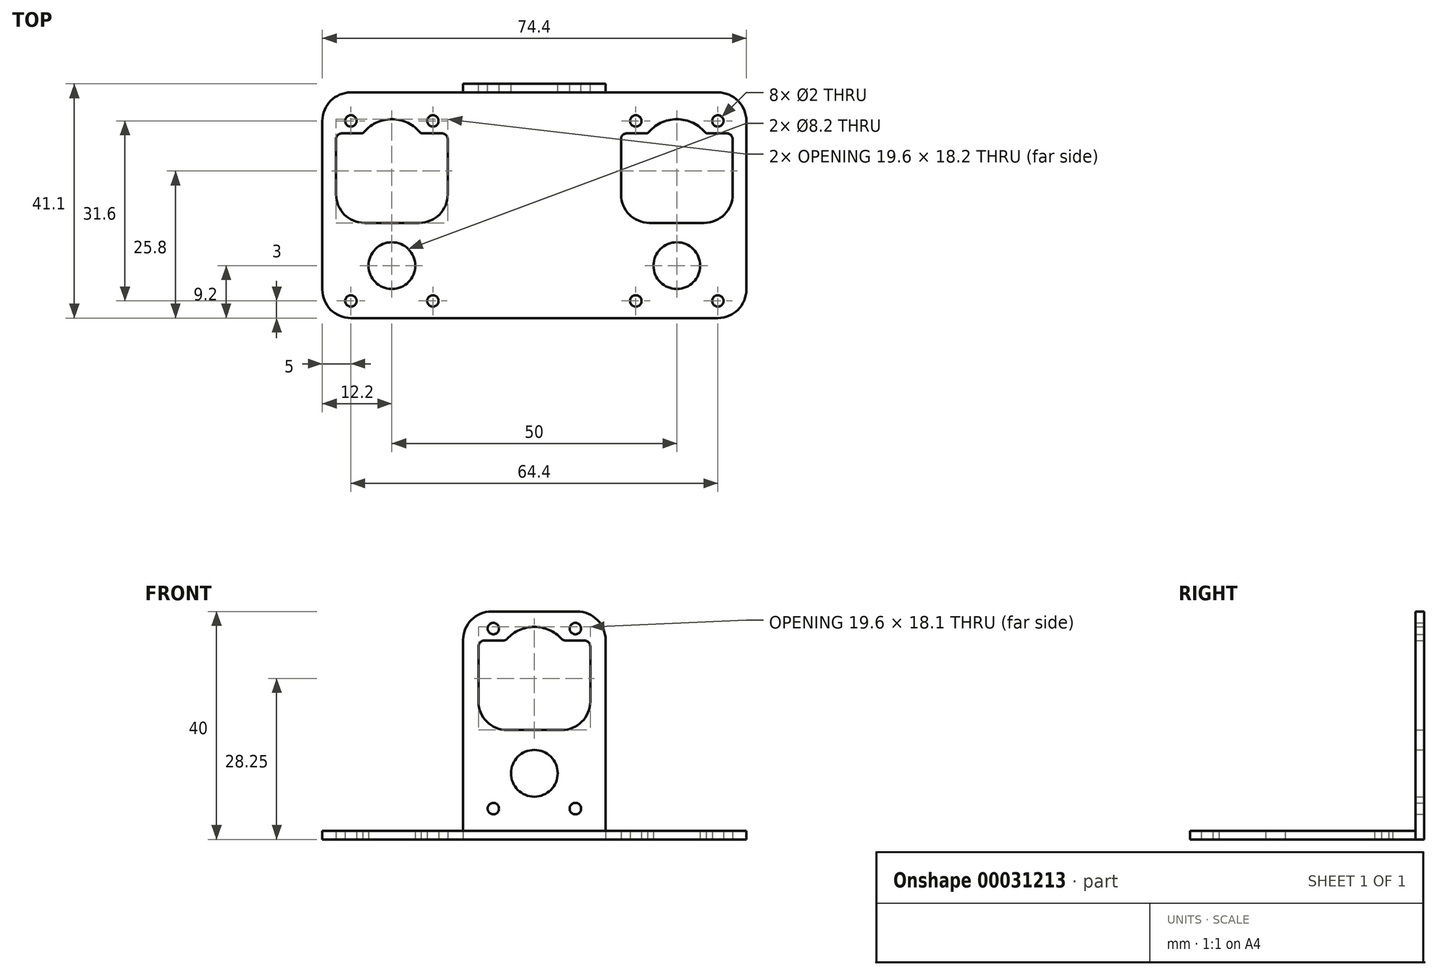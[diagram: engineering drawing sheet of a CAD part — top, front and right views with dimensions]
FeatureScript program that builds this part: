
annotation { "Feature Type Name" : "Feature", "Feature Type Description" : "" }
export const myFeature = defineFeature(function(context is Context, id is Id, definition is map)
    precondition{}
    {
        {
            var Q0;
            Q0=qCreatedBy(makeId("Top.planeOp"),FACE);
            var sketch = newSketch(context, id + "F0", { "sketchPlane" : qUnion([Q0])});
            skLineSegment(sketch, "E0.bottom", {"start": v(37.2, -19.8) * mm, "end": v(-37.2, -19.8) * mm});
            skLineSegment(sketch, "E0.top", {"start": v(37.2, 19.8) * mm, "end": v(-37.2, 19.8) * mm});
            skLineSegment(sketch, "E0.left", {"start": v(37.2, -19.8) * mm, "end": v(37.2, 19.8) * mm});
            skLineSegment(sketch, "E0.right", {"start": v(-37.2, -19.8) * mm, "end": v(-37.2, 19.8) * mm});
            skPoint(sketch, "E0.middle", {"position": v(0, 0) * mm});
            skCircle(sketch, "E1", {"center": v(25, 8.6) * mm, "radius": 4.1 * mm, "construction": true});
            skCircle(sketch, "E2", {"center": v(32.2, 14.8) * mm, "radius": 1 * mm});
            skLineSegment(sketch, "E3.bottom", {"start": v(33.8, -14.6) * mm, "end": v(30.12, -14.6) * mm, "construction": true});
            skLineSegment(sketch, "E3.top", {"start": v(29.8, 1.1) * mm, "end": v(20.2, 1.1) * mm, "construction": true});
            skLineSegment(sketch, "E3.left", {"start": v(34.8, -13.6) * mm, "end": v(34.8, -3.9) * mm, "construction": true});
            skLineSegment(sketch, "E3.right", {"start": v(15.2, -13.6) * mm, "end": v(15.2, -3.9) * mm, "construction": true});
            skPoint(sketch, "E3.middle", {"position": v(25, -6.75) * mm});
            skCircle(sketch, "E4", {"center": v(32.2, -16.8) * mm, "radius": 1 * mm});
            skPoint(sketch, "E5.visualSharp", {"position": v(15.2, 1.1) * mm});
            skArc(sketch, "E5.filletArc", {"start": v(20.2, 1.1) * mm, "mid": v(16.66, -0.36) * mm, "end": v(15.2, -3.9) * mm, "construction": true});
            skPoint(sketch, "E6.visualSharp", {"position": v(34.8, 1.1) * mm});
            skArc(sketch, "E6.filletArc", {"start": v(34.8, -3.9) * mm, "mid": v(33.34, -0.36) * mm, "end": v(29.8, 1.1) * mm, "construction": true});
            skPoint(sketch, "E7.visualSharp", {"position": v(15.2, -14.6) * mm});
            skArc(sketch, "E7.filletArc", {"start": v(15.2, -13.6) * mm, "mid": v(15.5, -14.3) * mm, "end": v(16.2, -14.6) * mm, "construction": true});
            skPoint(sketch, "E8.visualSharp", {"position": v(34.8, -14.6) * mm});
            skArc(sketch, "E8.filletArc", {"start": v(33.8, -14.6) * mm, "mid": v(34.5, -14.3) * mm, "end": v(34.8, -13.6) * mm, "construction": true});
            skArc(sketch, "E9", {"start": v(19.88, -14.6) * mm, "mid": v(25, -17.1) * mm, "end": v(30.12, -14.6) * mm, "construction": true});
            skLineSegment(sketch, "E10.trimOffspring", {"start": v(19.88, -14.6) * mm, "end": v(16.2, -14.6) * mm, "construction": true});
            skLineSegment(sketch, "E11", {"start": v(25, 19.8) * mm, "end": v(25, -19.8) * mm, "construction": true});
            skCircle(sketch, "E12.MirrorC", {"center": v(17.8, 14.8) * mm, "radius": 1 * mm});
            skCircle(sketch, "E13.MirrorC", {"center": v(17.8, -16.8) * mm, "radius": 1 * mm});
            skLineSegment(sketch, "E14", {"start": v(32.2, 14.8) * mm, "end": v(32.2, -16.8) * mm, "construction": true});
            skLineSegment(sketch, "E15", {"start": v(32.2, -1) * mm, "end": v(0, -1) * mm, "construction": true});
            skArc(sketch, "E16.MirrorCS", {"start": v(15.2, 11.6) * mm, "mid": v(15.5, 12.3) * mm, "end": v(16.2, 12.6) * mm});
            skArc(sketch, "E17.MirrorCS", {"start": v(33.8, 12.6) * mm, "mid": v(34.5, 12.3) * mm, "end": v(34.8, 11.6) * mm});
            skLineSegment(sketch, "E18.MirrorCS", {"start": v(15.2, 11.6) * mm, "end": v(15.2, 1.9) * mm});
            skLineSegment(sketch, "E19.MirrorCS", {"start": v(34.8, 11.6) * mm, "end": v(34.8, 1.9) * mm});
            skPoint(sketch, "E20.MirrorP", {"position": v(34.8, -3.1) * mm});
            skArc(sketch, "E21.MirrorCS", {"start": v(19.88, 12.6) * mm, "mid": v(25, 15.1) * mm, "end": v(30.12, 12.6) * mm});
            skPoint(sketch, "E22.MirrorP", {"position": v(15.2, -3.1) * mm});
            skPoint(sketch, "E23.MirrorP", {"position": v(25, 4.75) * mm});
            skCircle(sketch, "E24.MirrorC", {"center": v(25, -10.6) * mm, "radius": 4.1 * mm});
            skArc(sketch, "E25.MirrorCS", {"start": v(20.2, -3.1) * mm, "mid": v(16.66, -1.64) * mm, "end": v(15.2, 1.9) * mm});
            skLineSegment(sketch, "E26.MirrorCS", {"start": v(19.88, 12.6) * mm, "end": v(16.2, 12.6) * mm});
            skArc(sketch, "E27.MirrorCS", {"start": v(34.8, 1.9) * mm, "mid": v(33.34, -1.64) * mm, "end": v(29.8, -3.1) * mm});
            skPoint(sketch, "E28.MirrorP", {"position": v(34.8, 12.6) * mm});
            skLineSegment(sketch, "E29.MirrorCS", {"start": v(29.8, -3.1) * mm, "end": v(20.2, -3.1) * mm});
            skLineSegment(sketch, "E30.MirrorCS", {"start": v(33.8, 12.6) * mm, "end": v(30.12, 12.6) * mm});
            skPoint(sketch, "E31.MirrorP", {"position": v(15.2, 12.6) * mm});
            skArc(sketch, "E32.MirrorCS", {"start": v(-15.2, -13.6) * mm, "mid": v(-15.5, -14.3) * mm, "end": v(-16.2, -14.6) * mm, "construction": true});
            skArc(sketch, "E33.MirrorCS", {"start": v(-33.8, -14.6) * mm, "mid": v(-34.5, -14.3) * mm, "end": v(-34.8, -13.6) * mm, "construction": true});
            skArc(sketch, "E34.MirrorCS", {"start": v(-33.8, 12.6) * mm, "mid": v(-34.5, 12.3) * mm, "end": v(-34.8, 11.6) * mm});
            skArc(sketch, "E35.MirrorCS", {"start": v(-15.2, 11.6) * mm, "mid": v(-15.5, 12.3) * mm, "end": v(-16.2, 12.6) * mm});
            skPoint(sketch, "E36.MirrorP", {"position": v(-34.8, -14.6) * mm});
            skCircle(sketch, "E37.MirrorC", {"center": v(-25, 8.6) * mm, "radius": 4.1 * mm, "construction": true});
            skLineSegment(sketch, "E38.MirrorCS", {"start": v(-15.2, 11.6) * mm, "end": v(-15.2, 1.9) * mm});
            skArc(sketch, "E39.MirrorCS", {"start": v(-19.88, -14.6) * mm, "mid": v(-25, -17.1) * mm, "end": v(-30.12, -14.6) * mm, "construction": true});
            skCircle(sketch, "E40.MirrorC", {"center": v(-32.2, -16.8) * mm, "radius": 1 * mm});
            skLineSegment(sketch, "E41.MirrorCS", {"start": v(-33.8, -14.6) * mm, "end": v(-30.12, -14.6) * mm, "construction": true});
            skLineSegment(sketch, "E42.MirrorCS", {"start": v(-34.8, -13.6) * mm, "end": v(-34.8, -3.9) * mm, "construction": true});
            skCircle(sketch, "E43.MirrorC", {"center": v(-17.8, -16.8) * mm, "radius": 1 * mm});
            skPoint(sketch, "E44.MirrorP", {"position": v(-25, -6.75) * mm});
            skLineSegment(sketch, "E45.MirrorCS", {"start": v(-15.2, -13.6) * mm, "end": v(-15.2, -3.9) * mm, "construction": true});
            skPoint(sketch, "E46.MirrorP", {"position": v(-34.8, 12.6) * mm});
            skLineSegment(sketch, "E47.MirrorCS", {"start": v(-32.2, 14.8) * mm, "end": v(-32.2, -16.8) * mm, "construction": true});
            skLineSegment(sketch, "E48.MirrorCS", {"start": v(-34.8, 11.6) * mm, "end": v(-34.8, 1.9) * mm});
            skLineSegment(sketch, "E49.MirrorCS", {"start": v(-33.8, 12.6) * mm, "end": v(-30.12, 12.6) * mm});
            skArc(sketch, "E50.MirrorCS", {"start": v(-20.2, -3.1) * mm, "mid": v(-16.66, -1.64) * mm, "end": v(-15.2, 1.9) * mm});
            skArc(sketch, "E51.MirrorCS", {"start": v(-19.88, 12.6) * mm, "mid": v(-25, 15.1) * mm, "end": v(-30.12, 12.6) * mm});
            skLineSegment(sketch, "E52.MirrorCS", {"start": v(-19.88, 12.6) * mm, "end": v(-16.2, 12.6) * mm});
            skArc(sketch, "E53.MirrorCS", {"start": v(-34.8, -3.9) * mm, "mid": v(-33.34, -0.36) * mm, "end": v(-29.8, 1.1) * mm, "construction": true});
            skPoint(sketch, "E54.MirrorP", {"position": v(-15.2, 1.1) * mm});
            skCircle(sketch, "E55.MirrorC", {"center": v(-32.2, 14.8) * mm, "radius": 1 * mm});
            skPoint(sketch, "E56.MirrorP", {"position": v(-34.8, 1.1) * mm});
            skPoint(sketch, "E57.MirrorP", {"position": v(-15.2, -3.1) * mm});
            skLineSegment(sketch, "E58.MirrorCS", {"start": v(-29.8, 1.1) * mm, "end": v(-20.2, 1.1) * mm, "construction": true});
            skLineSegment(sketch, "E59.MirrorCS", {"start": v(-29.8, -3.1) * mm, "end": v(-20.2, -3.1) * mm});
            skPoint(sketch, "E60.MirrorP", {"position": v(-34.8, -3.1) * mm});
            skArc(sketch, "E61.MirrorCS", {"start": v(-20.2, 1.1) * mm, "mid": v(-16.66, -0.36) * mm, "end": v(-15.2, -3.9) * mm, "construction": true});
            skCircle(sketch, "E62.MirrorC", {"center": v(-25, -10.6) * mm, "radius": 4.1 * mm});
            skPoint(sketch, "E63.MirrorP", {"position": v(-15.2, -14.6) * mm});
            skPoint(sketch, "E64.MirrorP", {"position": v(-15.2, 12.6) * mm});
            skPoint(sketch, "E65.MirrorP", {"position": v(-25, 4.75) * mm});
            skArc(sketch, "E66.MirrorCS", {"start": v(-34.8, 1.9) * mm, "mid": v(-33.34, -1.64) * mm, "end": v(-29.8, -3.1) * mm});
            skCircle(sketch, "E67.MirrorC", {"center": v(-17.8, 14.8) * mm, "radius": 1 * mm});
            skLineSegment(sketch, "E68.MirrorCS", {"start": v(-19.88, -14.6) * mm, "end": v(-16.2, -14.6) * mm, "construction": true});
            skSolve(sketch);
        }
        {
            var Q0;
            Q0=qSketchRegion(id+"F0",true);
            extrude(context, id + "F1", {"entities" : qUnion([Q0]), "depth" : 1.5 * mm});
        }
        {
            var Q0;
            Q0=qCreatedBy(makeId("Top.planeOp"),FACE);
            var sketch = newSketch(context, id + "F2", { "sketchPlane" : qUnion([Q0])});
            skLineSegment(sketch, "E69.bottom", {"start": v(12.5, 19.8) * mm, "end": v(-12.5, 19.8) * mm});
            skLineSegment(sketch, "E69.top", {"start": v(12.5, 21.3) * mm, "end": v(-12.5, 21.3) * mm});
            skLineSegment(sketch, "E69.left", {"start": v(12.5, 19.8) * mm, "end": v(12.5, 21.3) * mm});
            skLineSegment(sketch, "E69.right", {"start": v(-12.5, 19.8) * mm, "end": v(-12.5, 21.3) * mm});
            skPoint(sketch, "E69.middle", {"position": v(0, 20.55) * mm});
            skLineSegment(sketch, "E70.0", {"start": v(37.2, 19.8) * mm, "end": v(-37.2, 19.8) * mm, "construction": true});
            skSolve(sketch);
        }
        {
            var Q0;
            Q0=qSketchRegion(id+"F2",true);
            extrude(context, id + "F3", {"entities" : qUnion([Q0]), "operationType" : NewBodyOperationType.ADD, "depth" : 40 * mm});
        }
        {
            var Q0;
            Q0=makeQuery(id+"F3.opExtrude","SWEPT_FACE",FACE,{"disambiguationData":[OSD([sQuery(id+"F2.wireOp",EDGE,"E69.top")])]});
            var sketch = newSketch(context, id + "F4", { "sketchPlane" : qUnion([Q0])});
            skLineSegment(sketch, "E71", {"start": v(-12.5, 20) * mm, "end": v(12.5, 20) * mm, "construction": true});
            skCircle(sketch, "E72", {"center": v(7.2, 37) * mm, "radius": 1 * mm});
            skCircle(sketch, "E73", {"center": v(7.2, 5.4) * mm, "radius": 1 * mm});
            skCircle(sketch, "E74", {"center": v(0, 11.6) * mm, "radius": 4.1 * mm});
            skLineSegment(sketch, "E75.bottom", {"start": v(8.8, 34.9) * mm, "end": v(5.5, 34.9) * mm});
            skLineSegment(sketch, "E75.top", {"start": v(4.8, 19.2) * mm, "end": v(-4.8, 19.2) * mm});
            skLineSegment(sketch, "E75.left", {"start": v(9.8, 33.9) * mm, "end": v(9.8, 24.2) * mm});
            skLineSegment(sketch, "E75.right", {"start": v(-9.8, 33.9) * mm, "end": v(-9.8, 24.2) * mm});
            skPoint(sketch, "E75.middle", {"position": v(0, 27.05) * mm});
            skPoint(sketch, "E76.visualSharp", {"position": v(-9.8, 19.2) * mm});
            skArc(sketch, "E76.filletArc", {"start": v(-9.8, 24.2) * mm, "mid": v(-8.34, 20.66) * mm, "end": v(-4.8, 19.2) * mm});
            skPoint(sketch, "E77.visualSharp", {"position": v(9.8, 19.2) * mm});
            skArc(sketch, "E77.filletArc", {"start": v(4.8, 19.2) * mm, "mid": v(8.34, 20.66) * mm, "end": v(9.8, 24.2) * mm});
            skPoint(sketch, "E78.visualSharp", {"position": v(9.8, 34.9) * mm});
            skArc(sketch, "E78.filletArc", {"start": v(9.8, 33.9) * mm, "mid": v(9.5, 34.6) * mm, "end": v(8.8, 34.9) * mm});
            skPoint(sketch, "E79.visualSharp", {"position": v(-9.8, 34.9) * mm});
            skArc(sketch, "E79.filletArc", {"start": v(-8.8, 34.9) * mm, "mid": v(-9.5, 34.6) * mm, "end": v(-9.8, 33.9) * mm});
            skCircle(sketch, "E80.MirrorC", {"center": v(-7.2, 37) * mm, "radius": 1 * mm});
            skCircle(sketch, "E81.MirrorC", {"center": v(-7.2, 5.4) * mm, "radius": 1 * mm});
            skArc(sketch, "E82", {"start": v(4.77, 35.22) * mm, "mid": v(0, 37.3) * mm, "end": v(-4.77, 35.22) * mm});
            skLineSegment(sketch, "E83.trimOffspring", {"start": v(-5.5, 34.9) * mm, "end": v(-8.8, 34.9) * mm});
            skPoint(sketch, "E84.visualSharp", {"position": v(-5.04, 34.9) * mm});
            skArc(sketch, "E84.filletArc", {"start": v(-5.5, 34.9) * mm, "mid": v(-5.1, 34.98) * mm, "end": v(-4.77, 35.22) * mm});
            skPoint(sketch, "E85.visualSharp", {"position": v(5.04, 34.9) * mm});
            skArc(sketch, "E85.filletArc", {"start": v(4.77, 35.22) * mm, "mid": v(5.1, 34.98) * mm, "end": v(5.5, 34.9) * mm});
            skSolve(sketch);
        }
        {
            var Q0;
            Q0=qSketchRegion(id+"F4",true);
            extrude(context, id + "F5", {"entities" : qUnion([Q0]), "operationType" : NewBodyOperationType.REMOVE, "endBound" : BoundingType.UP_TO_NEXT, "oppositeDirection" : true, "depth" : 25 * mm});
        }
        {
            var Q0;
            Q0=makeQuery(id+"F1.opExtrude","SWEPT_EDGE",EDGE,{"disambiguationData":[OSD([sQuery(id+"F0.wireOp",EDGE,"E0.top"),sQuery(id+"F0.wireOp",EDGE,"E0.right")])]});
            var Q1;
            Q1=makeQuery(id+"F1.opExtrude","SWEPT_EDGE",EDGE,{"disambiguationData":[OSD([sQuery(id+"F0.wireOp",EDGE,"E0.bottom"),sQuery(id+"F0.wireOp",EDGE,"E0.right")])]});
            var Q2;
            Q2=makeQuery(id+"F1.opExtrude","SWEPT_EDGE",EDGE,{"disambiguationData":[OSD([sQuery(id+"F0.wireOp",EDGE,"E0.top"),sQuery(id+"F0.wireOp",EDGE,"E0.left")])]});
            var Q3;
            Q3=makeQuery(id+"F1.opExtrude","SWEPT_EDGE",EDGE,{"disambiguationData":[OSD([sQuery(id+"F0.wireOp",EDGE,"E0.bottom"),sQuery(id+"F0.wireOp",EDGE,"E0.left")])]});
            var Q4;
            Q4=makeQuery(id+"F3.opExtrude","CAP_EDGE",EDGE,{"disambiguationData":[OSD([sQuery(id+"F2.wireOp",EDGE,"E69.right")])],"isStart":false});
            var Q5;
            Q5=makeQuery(id+"F3.opExtrude","CAP_EDGE",EDGE,{"disambiguationData":[OSD([sQuery(id+"F2.wireOp",EDGE,"E69.left")])],"isStart":false});
            fillet(context, id + "F6", {"entities" : qUnion([Q0, Q1, Q2, Q3, Q4, Q5]), "radius" : 5 * mm, "tangentPropagation" : true, "allowEdgeOverflow" : false});
        }
    });
